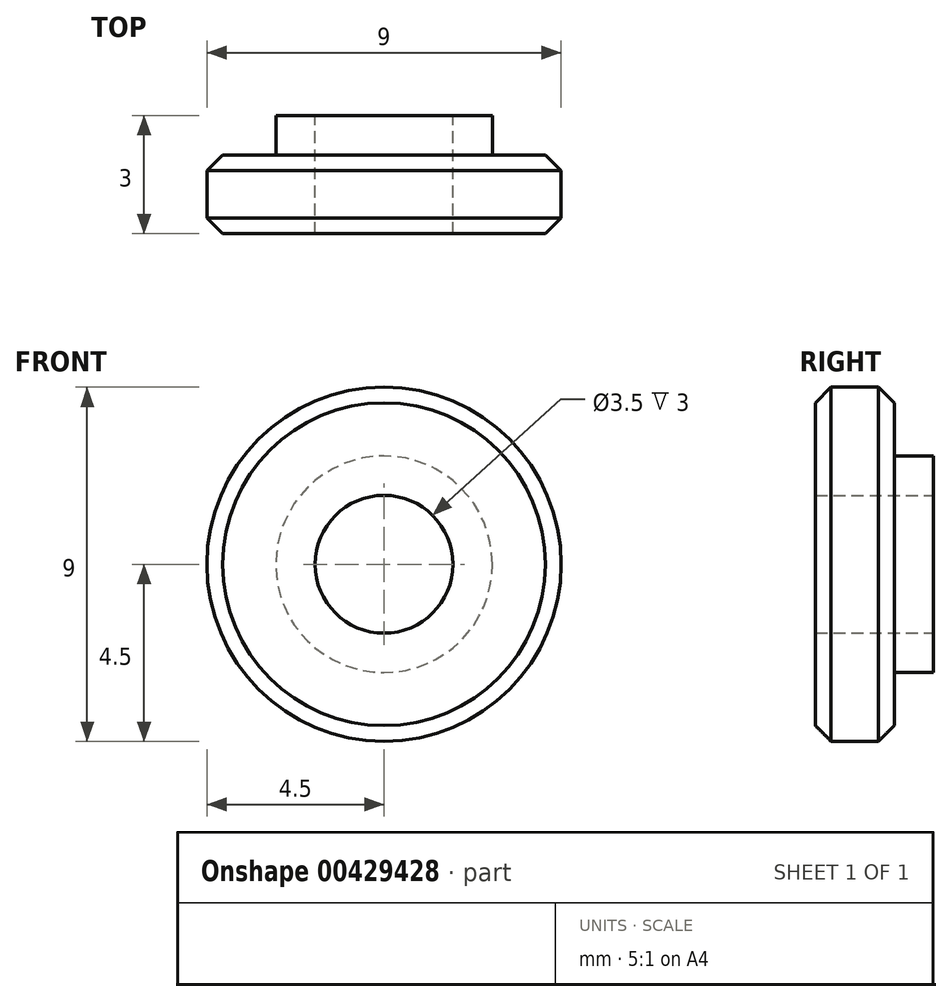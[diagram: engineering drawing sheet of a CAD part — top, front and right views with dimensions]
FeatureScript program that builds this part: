
annotation { "Feature Type Name" : "Feature", "Feature Type Description" : "" }
export const myFeature = defineFeature(function(context is Context, id is Id, definition is map)
    precondition{}
    {
        {
            var Q0;
            Q0=qCreatedBy(makeId("Front.planeOp"),FACE);
            var sketch = newSketch(context, id + "F0", { "sketchPlane" : qUnion([Q0])});
            skCircle(sketch, "E0", {"center": v(0, 0) * mm, "radius": 2.75 * mm});
            skCircle(sketch, "E1", {"center": v(0, 0) * mm, "radius": 1.75 * mm});
            skSolve(sketch);
        }
        {
            var Q0;
            Q0=makeQuery(id+"F0.imprint","IMPRINT",FACE,{"disambiguationData":[TD([[makeQuery(id+"F0.imprint","IMPRINT",EDGE,{"derivedFrom":sQuery(id+"F0.wireOp",EDGE,"E0")}),1.0]])]});
            extrude(context, id + "F1", {"entities" : qUnion([Q0]), "depth" : 1 * mm});
        }
        {
            var Q0;
            Q0=makeQuery(id+"F1.opExtrude","CAP_FACE",FACE,{"disambiguationData":[OSD([sQuery(id+"F0.wireOp",EDGE,"E0"),sQuery(id+"F0.wireOp",EDGE,"E1")])],"isStart":false});
            var sketch = newSketch(context, id + "F2", { "sketchPlane" : qUnion([Q0])});
            skCircle(sketch, "E2", {"center": v(0, 0) * mm, "radius": 1.75 * mm});
            skCircle(sketch, "E3", {"center": v(0, 0) * mm, "radius": 4.5 * mm});
            skSolve(sketch);
        }
        {
            var Q0;
            Q0=makeQuery(id+"F2.imprint","IMPRINT",FACE,{"disambiguationData":[TD([[makeQuery(id+"F2.imprint","IMPRINT",EDGE,{"derivedFrom":sQuery(id+"F2.wireOp",EDGE,"E2")}),-1.0]])]});
            var Q1;
            Q1=makeQuery(id+"F2.imprint","IMPRINT",FACE,{"disambiguationData":[TD([[makeQuery(id+"F2.imprint","IMPRINT",EDGE,{"derivedFrom":sQuery(id+"F2.wireOp",EDGE,"E3")}),1.0]])]});
            extrude(context, id + "F3", {"entities" : qUnion([Q0, Q1]), "operationType" : NewBodyOperationType.ADD, "depth" : 2 * mm});
        }
        {
            var Q0;
            Q0=makeQuery(id+"F3.opExtrude","CAP_EDGE",EDGE,{"disambiguationData":[OSD([sQuery(id+"F2.wireOp",EDGE,"E3")])],"isStart":false});
            var Q1;
            Q1=makeQuery(id+"F3.opExtrude","CAP_EDGE",EDGE,{"disambiguationData":[OSD([sQuery(id+"F2.wireOp",EDGE,"E3")])],"isStart":true});
            chamfer(context, id + "F4", {"entities" : qUnion([Q0, Q1]), "width" : 0.4 * mm, "tangentPropagation" : true});
        }
    });
